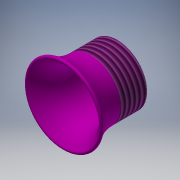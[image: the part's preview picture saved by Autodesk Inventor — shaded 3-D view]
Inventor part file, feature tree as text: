
AUTODESK INVENTOR PART (.ipt)
format: ipt  version: 2018 (Build 220112000, 112)  size: 176,128 bytes
history: native  units: mm
features: revolve x1, thread x1, sketch x1
ambient origin geometry x8: Origin, YZ Plane, XZ Plane, XY Plane, X Axis, Y Axis, Z Axis, Center Point
bodies: Solid1 (feature_tree)
feature tree (3):
  revolve  "Revolution1"  [1 undecoded]
  thread  "Thread1"  [1 undecoded]
  sketch  "Sketch1"  dims[d0=8.28mm d1=5.87mm d2=3.5mm d4=4.5mm d5=4.0mm d6=0.5mm d7=6.362336mm d8=90.0deg d9=10.0mm d10=0.0mm]
note: 2 required parameter values undecoded (feature->parameter linkage not recoverable at this tier; creation-order binding heuristic only, values carry confidence <= 0.55)